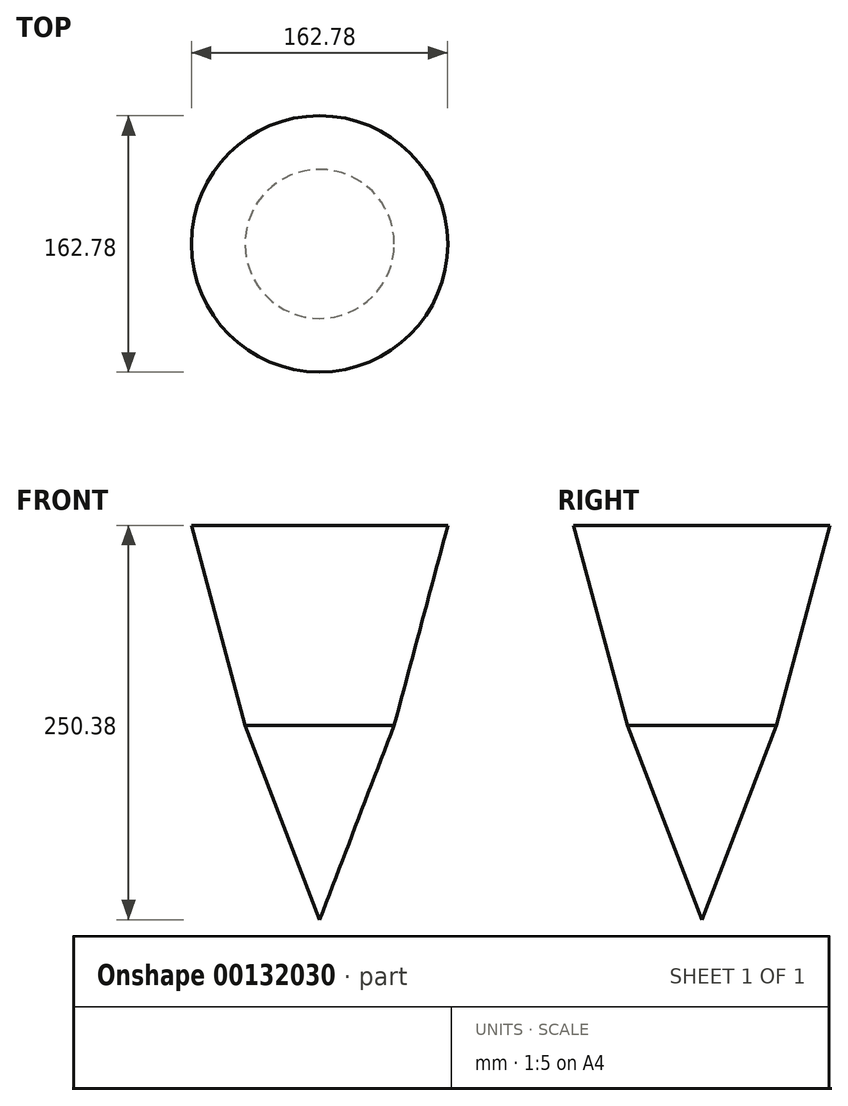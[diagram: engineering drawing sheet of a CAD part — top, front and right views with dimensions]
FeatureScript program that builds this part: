
annotation { "Feature Type Name" : "Feature", "Feature Type Description" : "" }
export const myFeature = defineFeature(function(context is Context, id is Id, definition is map)
    precondition{}
    {
        {
            var Q0;
            Q0=qCreatedBy(makeId("Top.planeOp"),FACE);
            var sketch = newSketch(context, id + "F0", { "sketchPlane" : qUnion([Q0])});
            skCircle(sketch, "E0", {"center": v(0, -15.83) * mm, "radius": 47.36 * mm});
            skSolve(sketch);
        }
        {
            var Q0;
            Q0=makeQuery(id+"F0.imprint","IMPRINT",FACE,{"disambiguationData":[TD([[makeQuery(id+"F0.imprint","IMPRINT",EDGE,{"derivedFrom":sQuery(id+"F0.wireOp",EDGE,"E0")}),1.0]])]});
            extrude(context, id + "F1", {"entities" : qUnion([Q0]), "depth" : 127 * mm, "hasDraft" : true, "draftAngle" : 15 * degree, "hasSecondDirection" : true, "secondDirectionOppositeDirection" : true, "secondDirectionDepth" : 127 * mm, "hasSecondDirectionDraft" : true, "secondDirectionDraftAngle" : 21 * degree, "secondDirectionDraftPullDirection" : true});
        }
    });
